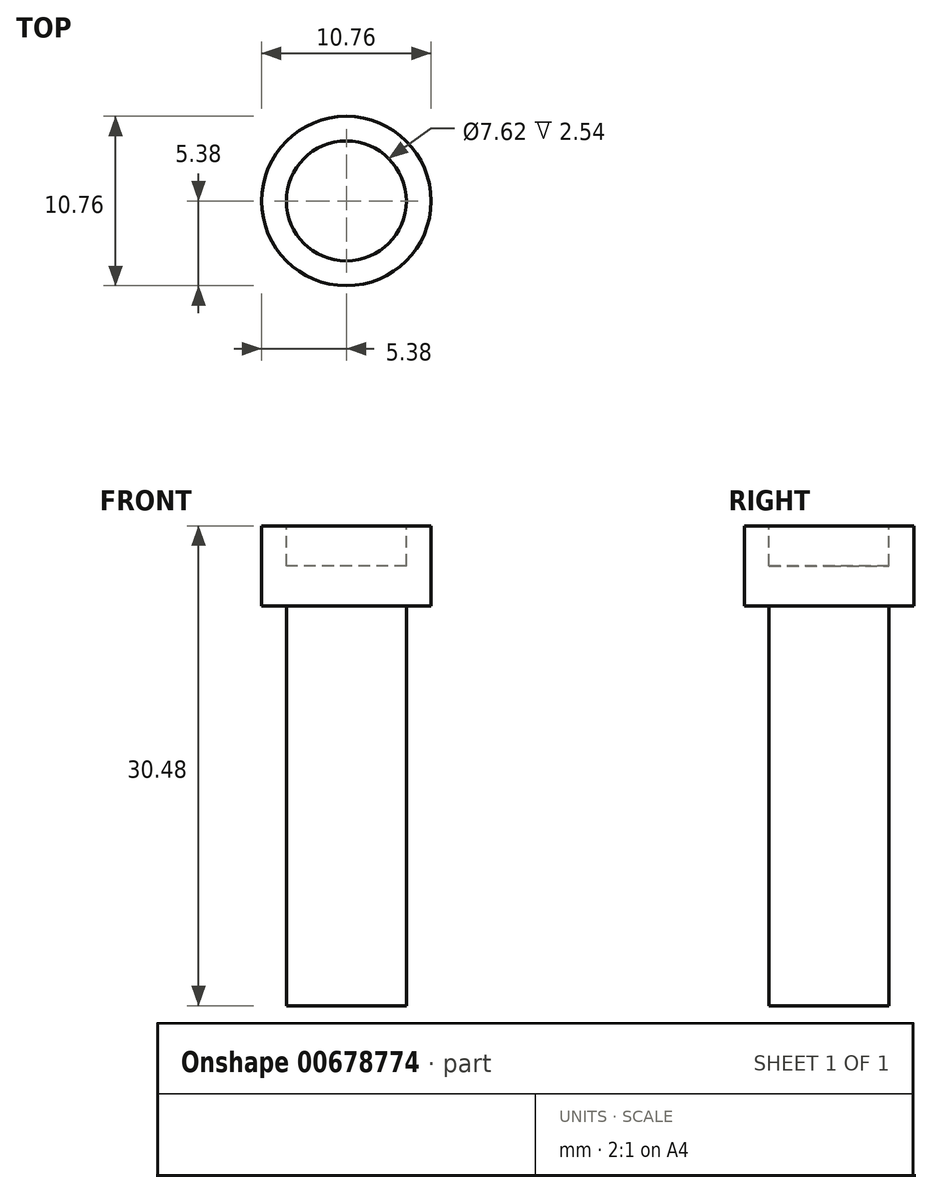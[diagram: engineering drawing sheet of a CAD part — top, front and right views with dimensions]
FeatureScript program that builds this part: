
annotation { "Feature Type Name" : "Feature", "Feature Type Description" : "" }
export const myFeature = defineFeature(function(context is Context, id is Id, definition is map)
    precondition{}
    {
        {
            var Q0;
            Q0=qCreatedBy(makeId("Top.planeOp"),FACE);
            var sketch = newSketch(context, id + "F0", { "sketchPlane" : qUnion([Q0])});
            skCircle(sketch, "E0", {"center": v(10.35, 0) * mm, "radius": 3.81 * mm});
            skSolve(sketch);
        }
        {
            var Q0;
            Q0 = qSketchRegion(id + "F0", true);
            extrude(context, id + "F1", {"entities" : qUnion([Q0]), "depth" : 25.4 * mm, "offsetDistance" : 25.4 * mm});
        }
        {
            var Q0;
            Q0=makeQuery(id+"F1.opExtrude","CAP_FACE",FACE,{"disambiguationData":[OSD([sQuery(id+"F0.wireOp",EDGE,"E0")])],"isStart":false});
            var sketch = newSketch(context, id + "F2", { "sketchPlane" : qUnion([Q0])});
            skCircle(sketch, "E1", {"center": v(10.35, 0) * mm, "radius": 5.38 * mm});
            skSolve(sketch);
        }
        {
            var Q0;
            Q0=makeQuery(id+"F2.imprint","IMPRINT",FACE,{"disambiguationData":[TD([[makeQuery(id+"F2.imprint","IMPRINT",EDGE,{"derivedFrom":sQuery(id+"F2.wireOp",EDGE,"E1")}),1.0]])]});
            var Q1;
            Q1=makeQuery(id+"F2.imprint","IMPRINT",FACE,{"disambiguationData":[TD([[makeQuery(id+"F2.imprint","IMPRINT",EDGE,{"derivedFrom":makeQuery(id+"F1.opExtrude","CAP_EDGE",EDGE,{"disambiguationData":[OSD([sQuery(id+"F0.wireOp",EDGE,"E0")])],"isStart":false})}),1.0]])]});
            extrude(context, id + "F3", {"entities" : qUnion([Q0, Q1]), "operationType" : NewBodyOperationType.ADD, "depth" : 5.08 * mm, "offsetDistance" : 25.4 * mm});
        }
        {
            var Q0;
            Q0=makeQuery(id+"F3.opExtrude","CAP_FACE",FACE,{"disambiguationData":[OSD([sQuery(id+"F2.wireOp",EDGE,"E1")])],"isStart":false});
            var sketch = newSketch(context, id + "F4", { "sketchPlane" : qUnion([Q0])});
            skCircle(sketch, "E2", {"center": v(10.35, 0) * mm, "radius": 3.81 * mm});
            skSolve(sketch);
        }
        {
            var Q0;
            Q0 = qSketchRegion(id + "F4", true);
            extrude(context, id + "F5", {"entities" : qUnion([Q0]), "operationType" : NewBodyOperationType.REMOVE, "oppositeDirection" : true, "depth" : 2.54 * mm, "offsetDistance" : 25.4 * mm});
        }
    });
